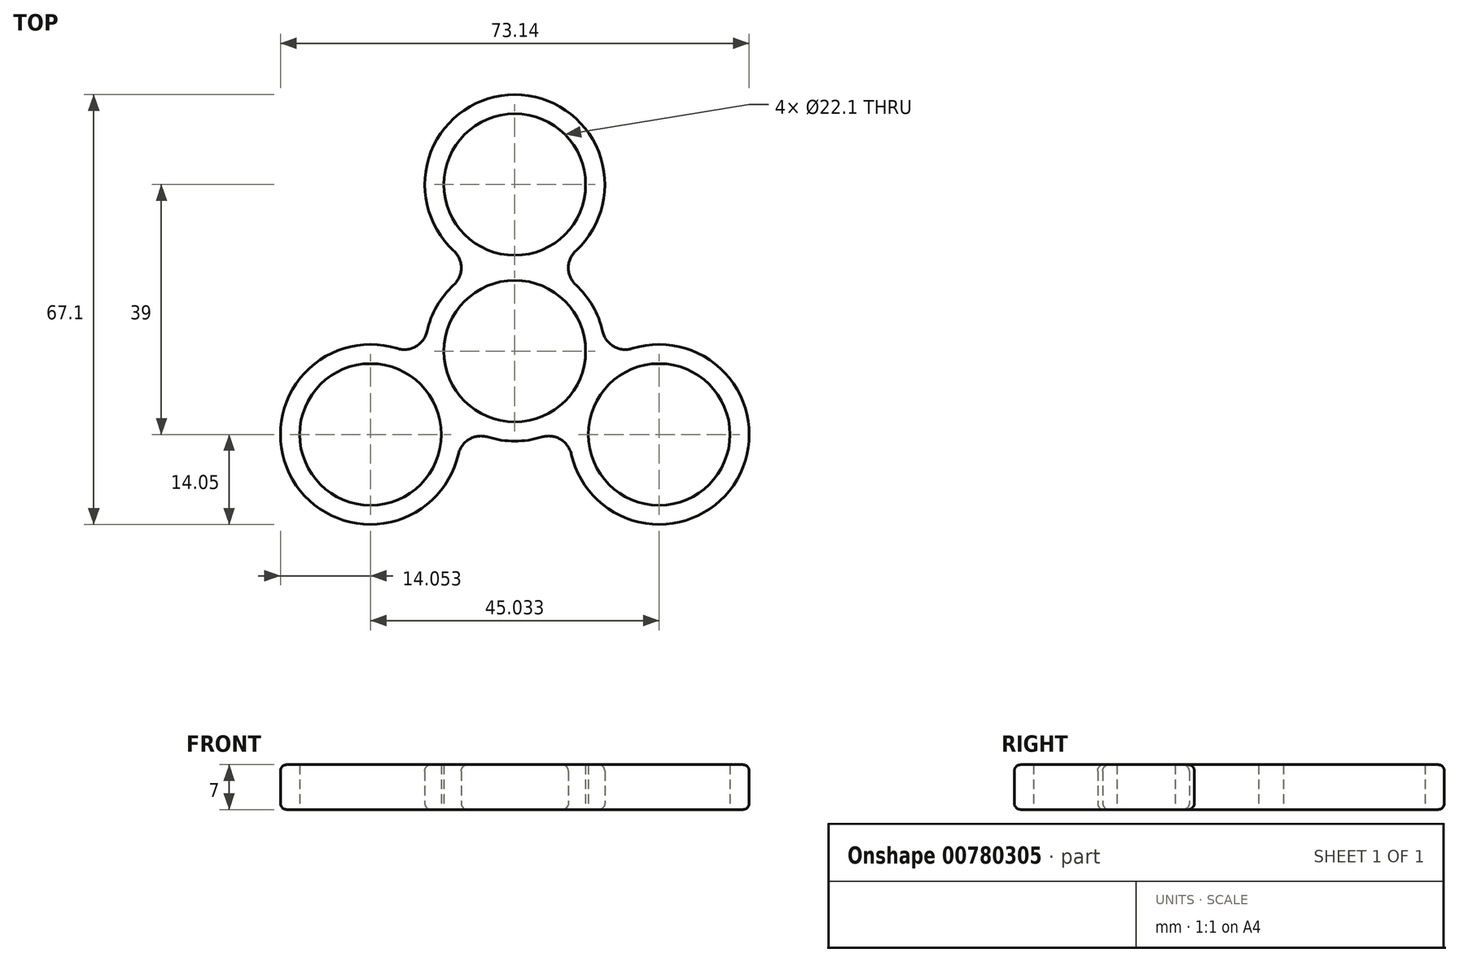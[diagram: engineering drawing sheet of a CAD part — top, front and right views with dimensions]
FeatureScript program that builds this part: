
annotation { "Feature Type Name" : "Feature", "Feature Type Description" : "" }
export const myFeature = defineFeature(function(context is Context, id is Id, definition is map)
    precondition{}
    {
        {
            var Q0;
            Q0=qCreatedBy(makeId("Top.planeOp"),FACE);
            var sketch = newSketch(context, id + "F0", { "sketchPlane" : qUnion([Q0])});
            skArc(sketch, "E0", {"start": v(-9.53, 10.32) * mm, "mid": v(-12.17, 7.03) * mm, "end": v(-13.7, 3.1) * mm});
            skCircle(sketch, "E1", {"center": v(0, 0) * mm, "radius": 11.05 * mm});
            skArc(sketch, "E2", {"start": v(9.53, 15.68) * mm, "mid": v(0, 40.05) * mm, "end": v(-9.53, 15.68) * mm});
            skCircle(sketch, "E3", {"center": v(0, 26) * mm, "radius": 11.05 * mm});
            skLineSegment(sketch, "E4", {"start": v(-12, 13) * mm, "end": v(12, 13) * mm, "construction": true});
            skLineSegment(sketch, "E5", {"start": v(0, 26) * mm, "end": v(0, 0) * mm, "construction": true});
            skPoint(sketch, "E6", {"position": v(0, 13) * mm});
            skArc(sketch, "E7", {"start": v(-9.53, 10.32) * mm, "mid": v(-8.36, 13) * mm, "end": v(-9.53, 15.68) * mm});
            skArc(sketch, "E8", {"start": v(9.53, 15.68) * mm, "mid": v(8.36, 13) * mm, "end": v(9.53, 10.32) * mm});
            skArc(sketch, "E9.1.0", {"start": v(-18.34, 0.42) * mm, "mid": v(-15.44, 0.74) * mm, "end": v(-13.7, 3.1) * mm});
            skPoint(sketch, "E9.1.1", {"position": v(-11.26, -6.5) * mm});
            skArc(sketch, "E9.1.2", {"start": v(-4.18, -13.42) * mm, "mid": v(-7.08, -13.74) * mm, "end": v(-8.81, -16.1) * mm});
            skLineSegment(sketch, "E9.1.3", {"start": v(-22.52, -13) * mm, "end": v(0, 0) * mm, "construction": true});
            skLineSegment(sketch, "E9.1.4", {"start": v(-5.26, -16.9) * mm, "end": v(-17.26, 3.9) * mm, "construction": true});
            skCircle(sketch, "E9.1.5", {"center": v(-22.52, -13) * mm, "radius": 11.05 * mm});
            skArc(sketch, "E9.1.6", {"start": v(-18.34, 0.42) * mm, "mid": v(-34.68, -20.03) * mm, "end": v(-8.81, -16.1) * mm});
            skArc(sketch, "E9.1.8", {"start": v(-4.18, -13.42) * mm, "mid": v(0, -14.05) * mm, "end": v(4.18, -13.42) * mm});
            skArc(sketch, "E9.2.0", {"start": v(8.81, -16.1) * mm, "mid": v(7.08, -13.74) * mm, "end": v(4.18, -13.42) * mm});
            skPoint(sketch, "E9.2.1", {"position": v(11.26, -6.5) * mm});
            skArc(sketch, "E9.2.2", {"start": v(13.7, 3.1) * mm, "mid": v(15.44, 0.74) * mm, "end": v(18.34, 0.42) * mm});
            skLineSegment(sketch, "E9.2.3", {"start": v(22.52, -13) * mm, "end": v(0, 0) * mm, "construction": true});
            skLineSegment(sketch, "E9.2.4", {"start": v(17.26, 3.9) * mm, "end": v(5.26, -16.9) * mm, "construction": true});
            skCircle(sketch, "E9.2.5", {"center": v(22.52, -13) * mm, "radius": 11.05 * mm});
            skArc(sketch, "E9.2.6", {"start": v(8.81, -16.1) * mm, "mid": v(34.68, -20.02) * mm, "end": v(18.34, 0.42) * mm});
            skArc(sketch, "E9.2.8", {"start": v(13.7, 3.1) * mm, "mid": v(12.17, 7.03) * mm, "end": v(9.53, 10.32) * mm});
            skSolve(sketch);
        }
        {
            var Q0;
            Q0 = qSketchRegion(id + "F0", true);
            extrude(context, id + "F1", {"entities" : qUnion([Q0]), "endBound" : BoundingType.SYMMETRIC, "depth" : 7 * mm, "offsetDistance" : 25 * mm});
        }
        {
            var Q0;
            Q0=makeQuery(id+"F1.opExtrude","CAP_EDGE",EDGE,{"disambiguationData":[OSD([sQuery(id+"F0.wireOp",EDGE,"E9.1.6")])],"isStart":false});
            var Q1;
            Q1=makeQuery(id+"F1.opExtrude","CAP_EDGE",EDGE,{"disambiguationData":[OSD([sQuery(id+"F0.wireOp",EDGE,"E9.1.6")])],"isStart":true});
            fillet(context, id + "F2", {"entities" : qUnion([Q0, Q1]), "radius" : 1 * mm, "tangentPropagation" : true, "allowEdgeOverflow" : false});
        }
    });
